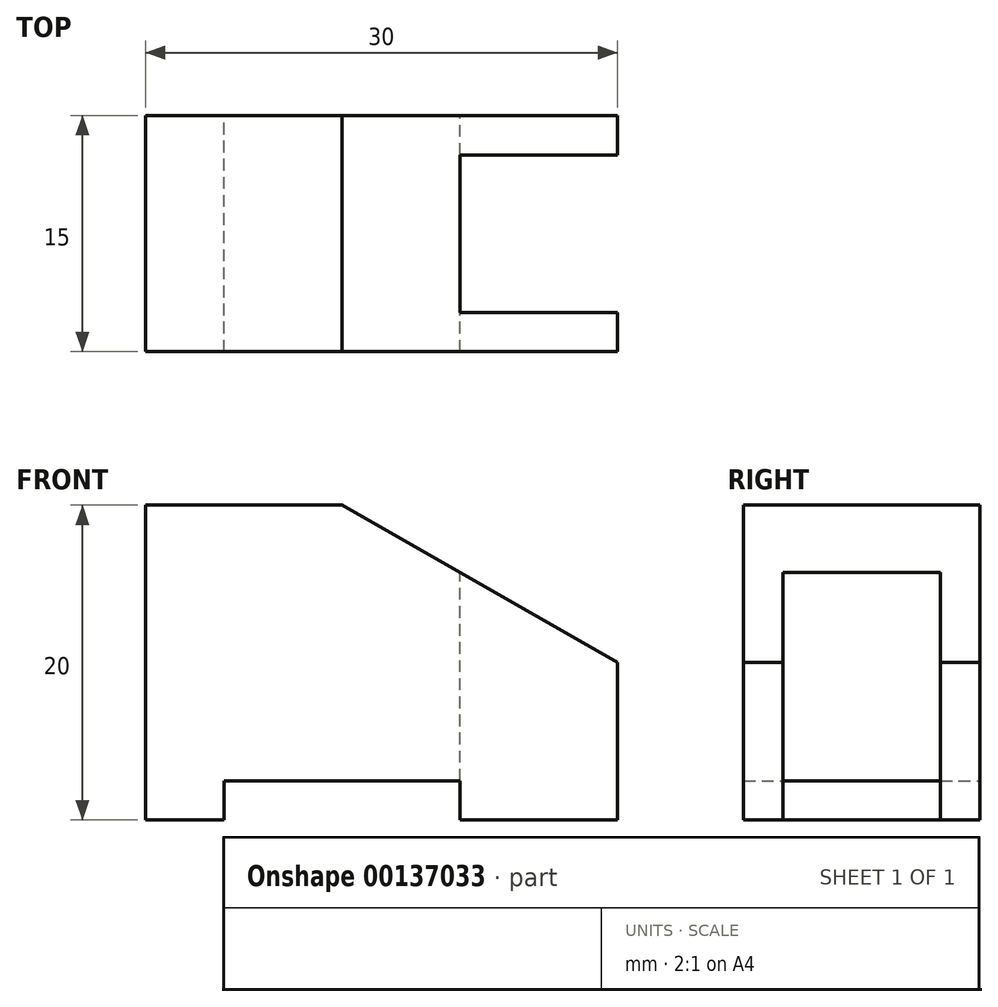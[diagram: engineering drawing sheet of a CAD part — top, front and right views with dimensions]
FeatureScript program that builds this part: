
annotation { "Feature Type Name" : "Feature", "Feature Type Description" : "" }
export const myFeature = defineFeature(function(context is Context, id is Id, definition is map)
    precondition{}
    {
        {
            var Q0;
            Q0=qCreatedBy(makeId("Front.planeOp"),FACE);
            var sketch = newSketch(context, id + "F0", { "sketchPlane" : qUnion([Q0])});
            skLineSegment(sketch, "E0", {"start": v(0, 0) * mm, "end": v(0, 20) * mm});
            skLineSegment(sketch, "E1", {"start": v(0, 20) * mm, "end": v(12.5, 20) * mm});
            skLineSegment(sketch, "E2", {"start": v(12.5, 20) * mm, "end": v(30, 10) * mm});
            skLineSegment(sketch, "E3", {"start": v(30, 10) * mm, "end": v(30, 0) * mm});
            skLineSegment(sketch, "E4", {"start": v(30, 0) * mm, "end": v(20, 0) * mm});
            skLineSegment(sketch, "E5", {"start": v(20, 0) * mm, "end": v(20, 2.5) * mm});
            skLineSegment(sketch, "E6", {"start": v(20, 2.5) * mm, "end": v(5, 2.5) * mm});
            skLineSegment(sketch, "E7", {"start": v(5, 2.5) * mm, "end": v(5, 0) * mm});
            skLineSegment(sketch, "E8", {"start": v(5, 0) * mm, "end": v(0, 0) * mm});
            skLineSegment(sketch, "E9", {"start": v(20, 2.5) * mm, "end": v(20, 15.71) * mm});
            skSolve(sketch);
        }
        {
            var Q0;
            Q0 = qSketchRegion(id + "F0", true);
            extrude(context, id + "F1", {"entities" : qUnion([Q0]), "endBound" : BoundingType.SYMMETRIC, "depth" : 15 * mm});
        }
        {
            var Q0;
            {var subQ0=sQuery(id+"F0.wireOp",EDGE,"E3");Q0=makeQuery(id+"F0.imprint","IMPRINT",FACE,{"disambiguationData":[TD([[makeQuery(id+"F0.imprint","IMPRINT",EDGE,{"derivedFrom":subQ0}),-1.0]])]});}
            extrude(context, id + "F2", {"entities" : qUnion([Q0]), "operationType" : NewBodyOperationType.REMOVE, "endBound" : BoundingType.SYMMETRIC, "oppositeDirection" : true, "depth" : 10 * mm});
        }
    });
